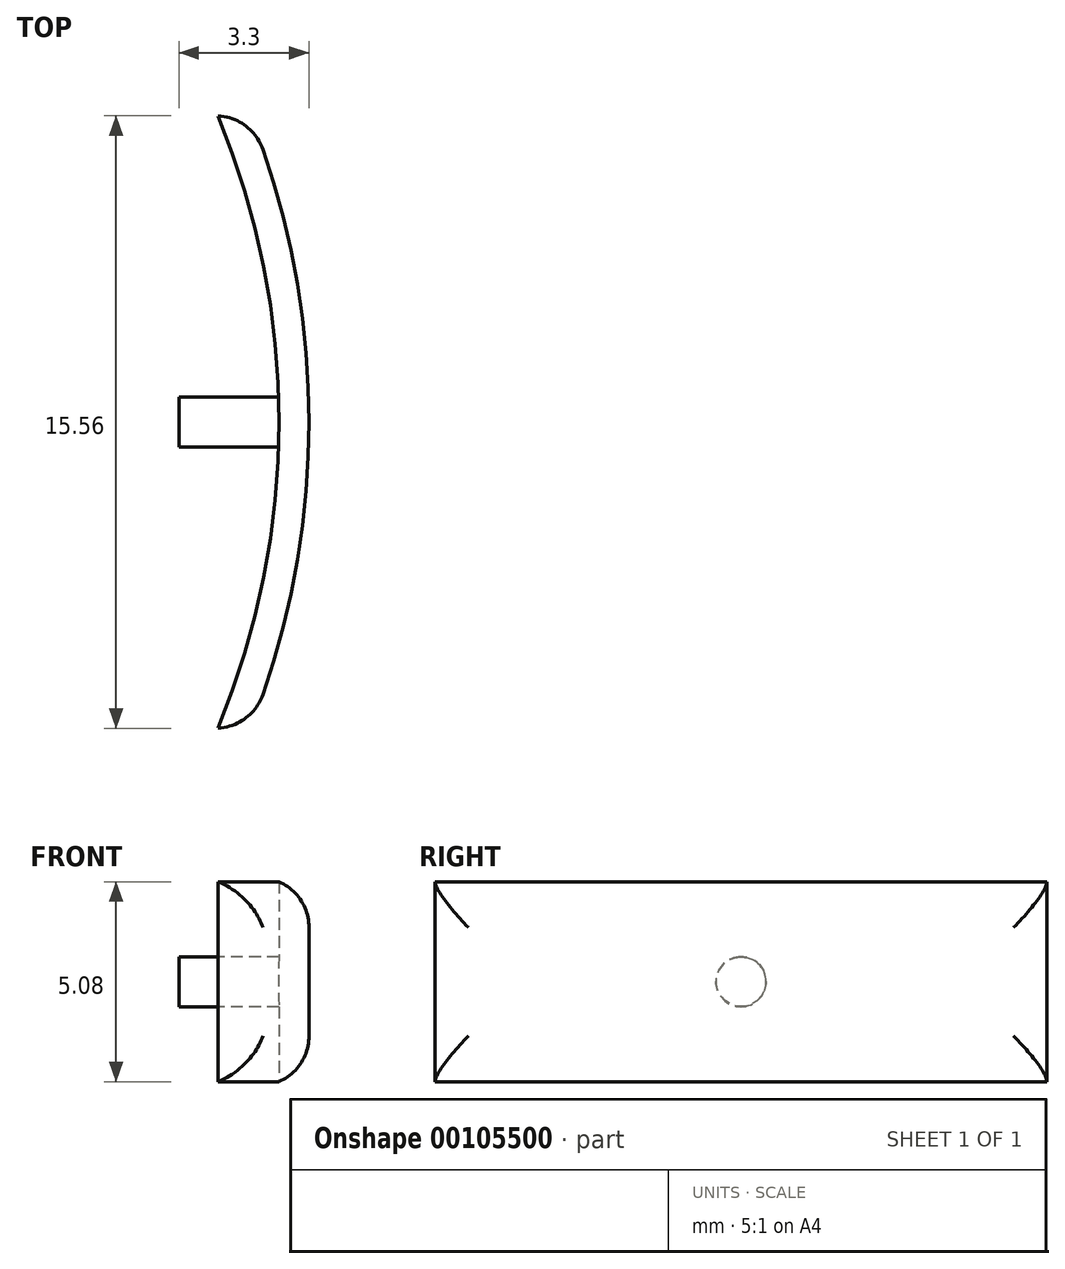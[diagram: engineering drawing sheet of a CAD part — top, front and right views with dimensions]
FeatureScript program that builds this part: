
annotation { "Feature Type Name" : "Feature", "Feature Type Description" : "" }
export const myFeature = defineFeature(function(context is Context, id is Id, definition is map)
    precondition{}
    {
        {
            var Q0;
            Q0=qCreatedBy(makeId("Top.planeOp"),FACE);
            var sketch = newSketch(context, id + "F0", { "sketchPlane" : qUnion([Q0])});
            skCircle(sketch, "E0", {"center": v(0, 0) * mm, "radius": 21.08 * mm});
            skCircle(sketch, "E1", {"center": v(0, 0) * mm, "radius": 20.32 * mm});
            skLineSegment(sketch, "E2", {"start": v(0, 0) * mm, "end": v(19.48, 8.07) * mm});
            skLineSegment(sketch, "E3", {"start": v(0, 0) * mm, "end": v(19.48, -8.07) * mm});
            skLineSegment(sketch, "E4", {"start": v(0, 0) * mm, "end": v(20.32, 0) * mm, "construction": true});
            skSolve(sketch);
        }
        {
            var Q0;
            {var subQ0=sQuery(id+"F0.wireOp",EDGE,"E2");var subQ1=sQuery(id+"F0.wireOp",EDGE,"E0");var subQ2=makeQuery(id+"F0.imprint","INTERSECT",VERTEX,{"derivedFrom":[subQ1,subQ0]});Q0=makeQuery(id+"F0.imprint","IMPRINT",FACE,{"disambiguationData":[TD([[makeQuery(id+"F0.imprint","IMPRINT",EDGE,{"disambiguationData":[TD([[subQ2,1.0]])],"derivedFrom":subQ1}),1.0]])]});}
            extrude(context, id + "F1", {"entities" : qUnion([Q0]), "depth" : 2.54 * mm, "hasSecondDirection" : true, "secondDirectionOppositeDirection" : true, "secondDirectionDepth" : 2.54 * mm});
        }
        {
            var Q0;
            Q0=makeQuery(id+"F1.opExtrude","SWEPT_FACE",FACE,{"disambiguationData":[OSD([sQuery(id+"F0.wireOp",EDGE,"E0")])]});
            fillet(context, id + "F2", {"entities" : qUnion([Q0]), "radius" : 1.27 * mm, "tangentPropagation" : true, "allowEdgeOverflow" : false});
        }
        {
            var Q0;
            Q0=qCreatedBy(makeId("Right.planeOp"),FACE);
            cPlane(context, id + "F3", {"entities" : qUnion([Q0]), "cplaneType" : CPlaneType.OFFSET, "offset" : 17.78 * mm, "width" : 152.4 * mm, "height" : 152.4 * mm});
        }
        {
            var Q0;
            Q0=qCreatedBy(id+"F3.planeOp",FACE);
            var sketch = newSketch(context, id + "F4", { "sketchPlane" : qUnion([Q0])});
            skCircle(sketch, "E5", {"center": v(0, 0) * mm, "radius": 0.64 * mm});
            skSolve(sketch);
        }
        {
            var Q0;
            Q0=makeQuery(id+"F4.imprint","IMPRINT",FACE,{"disambiguationData":[TD([[makeQuery(id+"F4.imprint","IMPRINT",EDGE,{"derivedFrom":sQuery(id+"F4.wireOp",EDGE,"E5")}),1.0]])]});
            extrude(context, id + "F5", {"entities" : qUnion([Q0]), "operationType" : NewBodyOperationType.ADD, "endBound" : BoundingType.UP_TO_NEXT, "depth" : 25.4 * mm});
        }
    });
